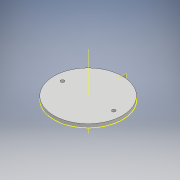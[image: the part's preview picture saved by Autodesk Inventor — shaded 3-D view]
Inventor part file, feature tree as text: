
AUTODESK INVENTOR PART (.ipt)
format: ipt  version: 2018 (Build 220112000, 112)  size: 103,424 bytes
history: native  units: mm
features: other x3, sketch x3, extrude x1, hole x1
ambient origin geometry x8: Origin, YZ Plane, XZ Plane, XY Plane, X Axis, Y Axis, Z Axis, Center Point
bodies: Body1 (feature_tree)
feature tree (8):
  other  "ソリッド1"
  extrude  "押し出し1"  Depth=200.0mm
  hole  "穴1"  [1 undecoded]
  other  "作業軸2"
  sketch  "スケッチ3"
  other  "作業平面1"
  sketch  "スケッチ1"
  sketch  "スケッチ2"
note: 1 required parameter value undecoded (feature->parameter linkage not recoverable at this tier; creation-order binding heuristic only, values carry confidence <= 0.55)
